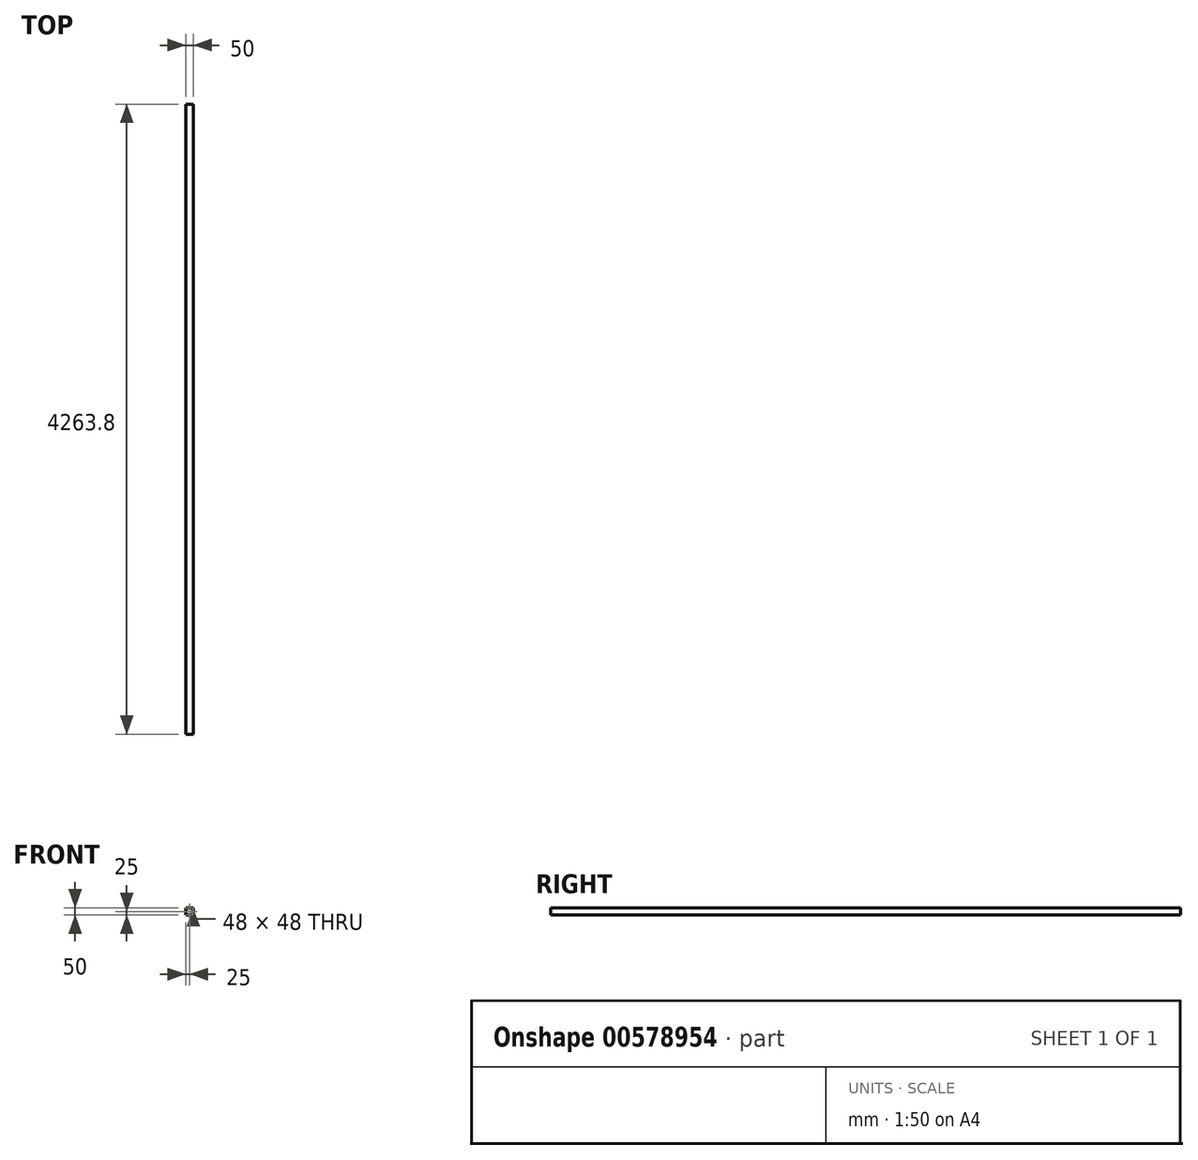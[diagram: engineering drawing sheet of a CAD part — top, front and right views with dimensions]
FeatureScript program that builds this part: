
annotation { "Feature Type Name" : "Feature", "Feature Type Description" : "" }
export const myFeature = defineFeature(function(context is Context, id is Id, definition is map)
    precondition{}
    {
        {
            var Q0;
            Q0=qCreatedBy(makeId("Front.planeOp"),FACE);
            var sketch = newSketch(context, id + "F0", { "sketchPlane" : qUnion([Q0])});
            skLineSegment(sketch, "E0.bottom", {"start": v(25, 25) * mm, "end": v(-25, 25) * mm});
            skLineSegment(sketch, "E0.top", {"start": v(25, -25) * mm, "end": v(-25, -25) * mm});
            skLineSegment(sketch, "E0.left", {"start": v(25, 25) * mm, "end": v(25, -25) * mm});
            skLineSegment(sketch, "E0.right", {"start": v(-25, 25) * mm, "end": v(-25, -25) * mm});
            skPoint(sketch, "E0.middle", {"position": v(0, 0) * mm});
            skLineSegment(sketch, "E1.bottom", {"start": v(24, 24) * mm, "end": v(-24, 24) * mm});
            skLineSegment(sketch, "E1.top", {"start": v(24, -24) * mm, "end": v(-24, -24) * mm});
            skLineSegment(sketch, "E1.left", {"start": v(24, 24) * mm, "end": v(24, -24) * mm});
            skLineSegment(sketch, "E1.right", {"start": v(-24, 24) * mm, "end": v(-24, -24) * mm});
            skSolve(sketch);
        }
        {
            var Q0;
            Q0=makeQuery(id+"F0.imprint","IMPRINT",FACE,{"disambiguationData":[TD([[makeQuery(id+"F0.imprint","IMPRINT",EDGE,{"derivedFrom":sQuery(id+"F0.wireOp",EDGE,"E0.bottom")}),1.0]])]});
            extrude(context, id + "F1", {"entities" : qUnion([Q0]), "endBound" : BoundingType.SYMMETRIC, "depth" : 4263.8 * mm, "offsetDistance" : 25 * mm});
        }
    });
